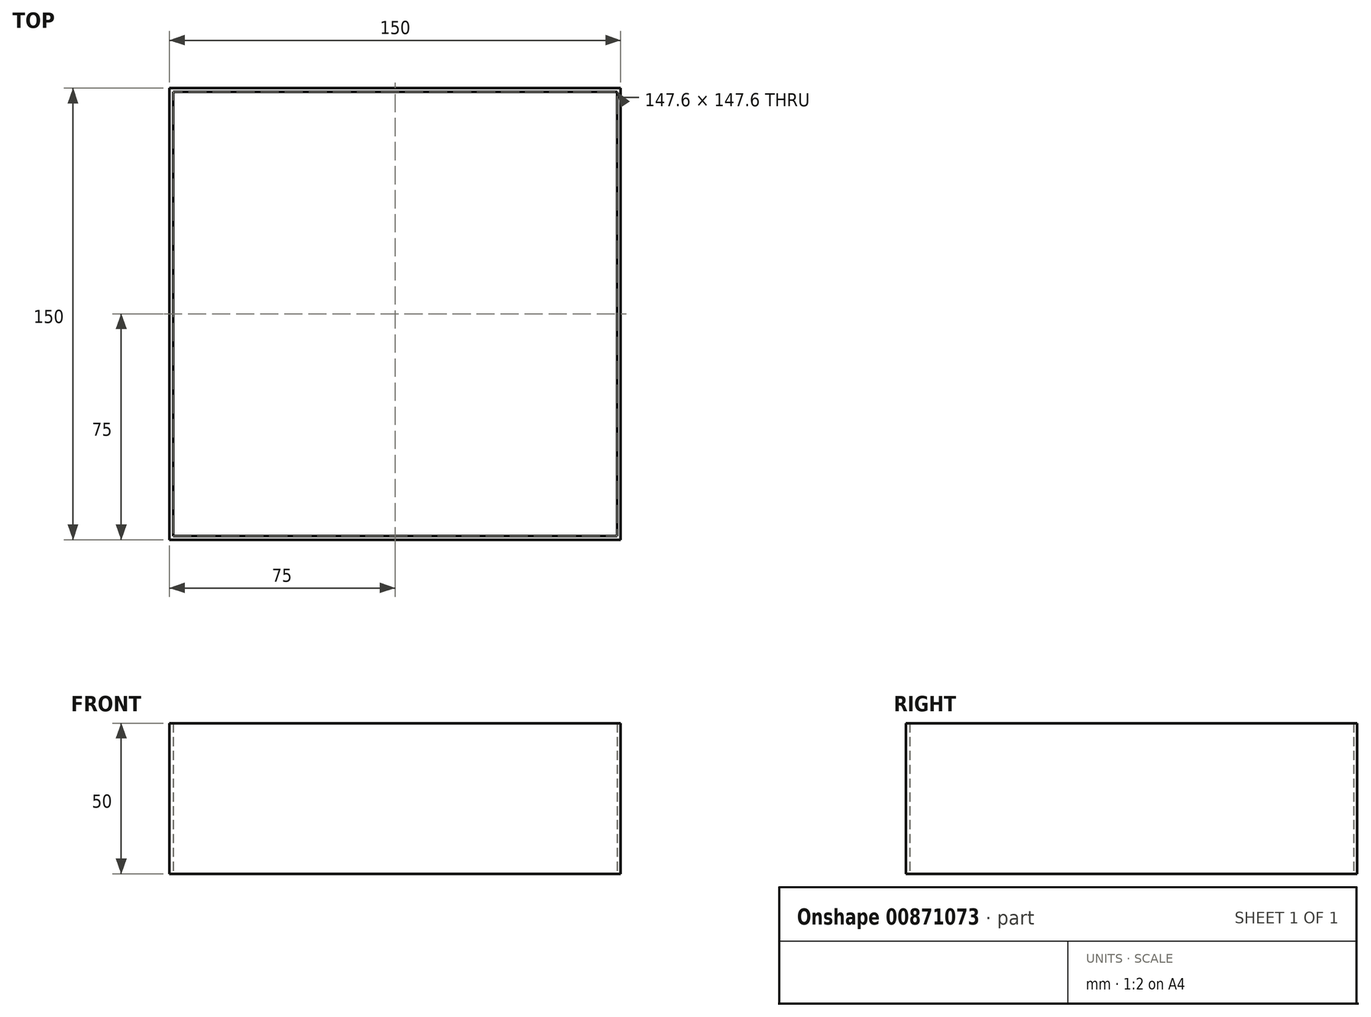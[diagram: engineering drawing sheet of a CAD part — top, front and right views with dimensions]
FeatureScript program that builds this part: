
annotation { "Feature Type Name" : "Feature", "Feature Type Description" : "" }
export const myFeature = defineFeature(function(context is Context, id is Id, definition is map)
    precondition{}
    {
        {
            var Q0;
            Q0=qCreatedBy(makeId("Top.planeOp"),FACE);
            var sketch = newSketch(context, id + "F0", { "sketchPlane" : qUnion([Q0])});
            skLineSegment(sketch, "E0.bottom", {"start": v(0, 0) * mm, "end": v(150, 0) * mm});
            skLineSegment(sketch, "E0.top", {"start": v(0, 150) * mm, "end": v(150, 150) * mm});
            skLineSegment(sketch, "E0.left", {"start": v(0, 0) * mm, "end": v(0, 150) * mm});
            skLineSegment(sketch, "E0.right", {"start": v(150, 0) * mm, "end": v(150, 150) * mm});
            skLineSegment(sketch, "E1.0", {"start": v(1.2, 1.2) * mm, "end": v(1.2, 148.8) * mm});
            skLineSegment(sketch, "E1.1", {"start": v(1.2, 1.2) * mm, "end": v(148.8, 1.2) * mm});
            skLineSegment(sketch, "E1.2", {"start": v(148.8, 1.2) * mm, "end": v(148.8, 148.8) * mm});
            skLineSegment(sketch, "E1.3", {"start": v(1.2, 148.8) * mm, "end": v(148.8, 148.8) * mm});
            skSolve(sketch);
        }
        {
            var Q0;
            Q0=makeQuery(id+"F0.imprint","IMPRINT",FACE,{"disambiguationData":[TD([[makeQuery(id+"F0.imprint","IMPRINT",EDGE,{"derivedFrom":sQuery(id+"F0.wireOp",EDGE,"E0.bottom")}),1.0]])]});
            extrude(context, id + "F1", {"entities" : qUnion([Q0]), "depth" : 50 * mm, "offsetDistance" : 25 * mm});
        }
    });
